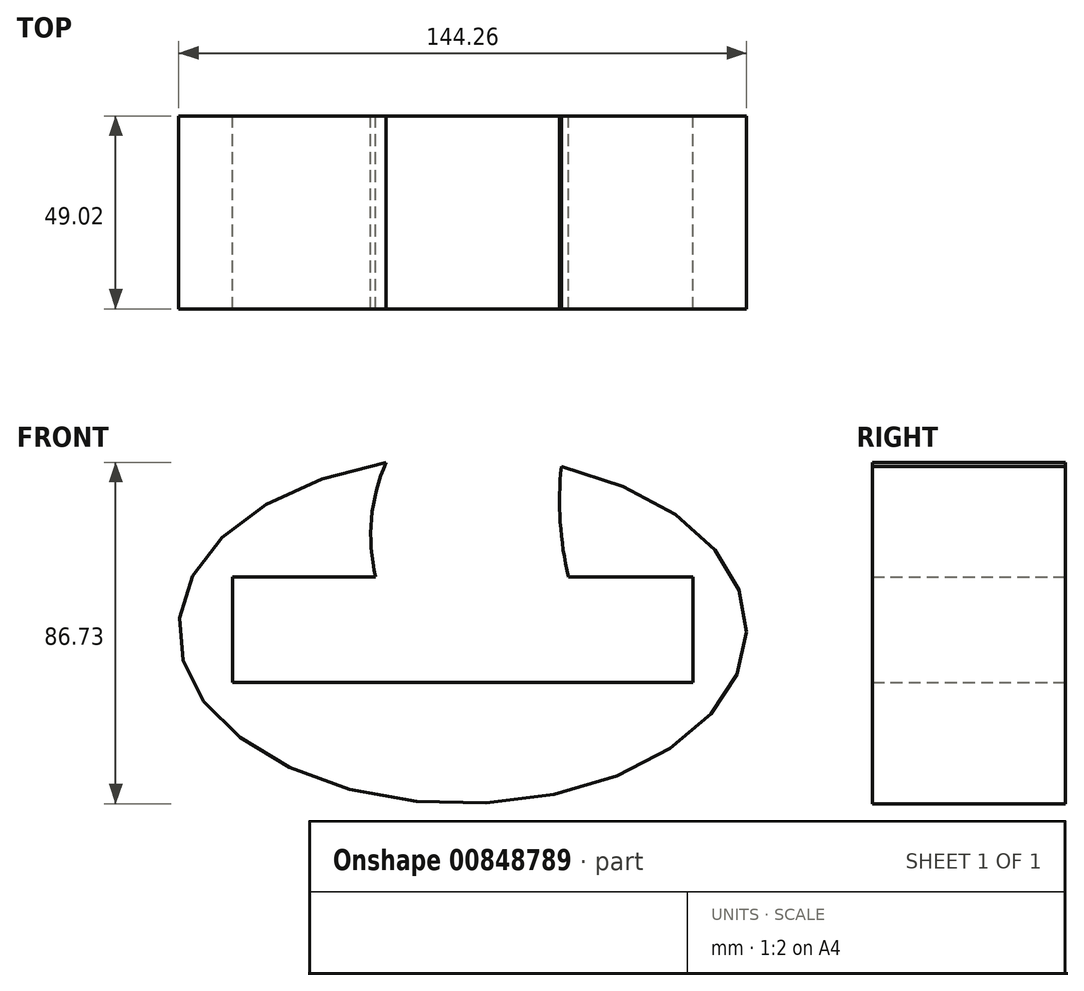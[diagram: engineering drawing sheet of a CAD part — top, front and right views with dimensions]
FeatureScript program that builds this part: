
annotation { "Feature Type Name" : "Feature", "Feature Type Description" : "" }
export const myFeature = defineFeature(function(context is Context, id is Id, definition is map)
    precondition{}
    {
        {
            var Q0;
            Q0=qCreatedBy(makeId("Front.planeOp"),FACE);
            var sketch = newSketch(context, id + "F0", { "sketchPlane" : qUnion([Q0])});
            skEllipse(sketch, "E0", {"center": v(0, 0) * mm, "majorRadius": 72.13 * mm, "minorRadius": 44.18 * mm, "majorAxis": v(-1, 0)});
            skLineSegment(sketch, "E1.bottom", {"start": v(-58.5, -13.39) * mm, "end": v(58.5, -13.39) * mm});
            skLineSegment(sketch, "E1.top", {"start": v(-58.5, 13.39) * mm, "end": v(58.5, 13.39) * mm});
            skLineSegment(sketch, "E1.left", {"start": v(-58.5, -13.39) * mm, "end": v(-58.5, 13.39) * mm});
            skLineSegment(sketch, "E1.right", {"start": v(58.5, -13.39) * mm, "end": v(58.5, 13.39) * mm});
            skArc(sketch, "E2", {"start": v(-19.43, 42.55) * mm, "mid": v(-23.16, 28.18) * mm, "end": v(-22.1, 13.39) * mm});
            skArc(sketch, "E3", {"start": v(25.06, 41.43) * mm, "mid": v(24.8, 27.33) * mm, "end": v(26.92, 13.39) * mm});
            skArc(sketch, "E4", {"start": v(3.46, 44.13) * mm, "mid": v(0.02, 28.95) * mm, "end": v(0, 13.39) * mm});
            skSolve(sketch);
        }
        {
            var Q0;
            Q0=makeQuery(id+"F0.imprint","IMPRINT",FACE,{"disambiguationData":[TD([[makeQuery(id+"F0.imprint","IMPRINT",EDGE,{"derivedFrom":sQuery(id+"F0.wireOp",EDGE,"E1.bottom")}),-1.0]])]});
            extrude(context, id + "F1", {"entities" : qUnion([Q0]), "depth" : 49.02 * mm, "offsetDistance" : 25.4 * mm});
        }
    });
